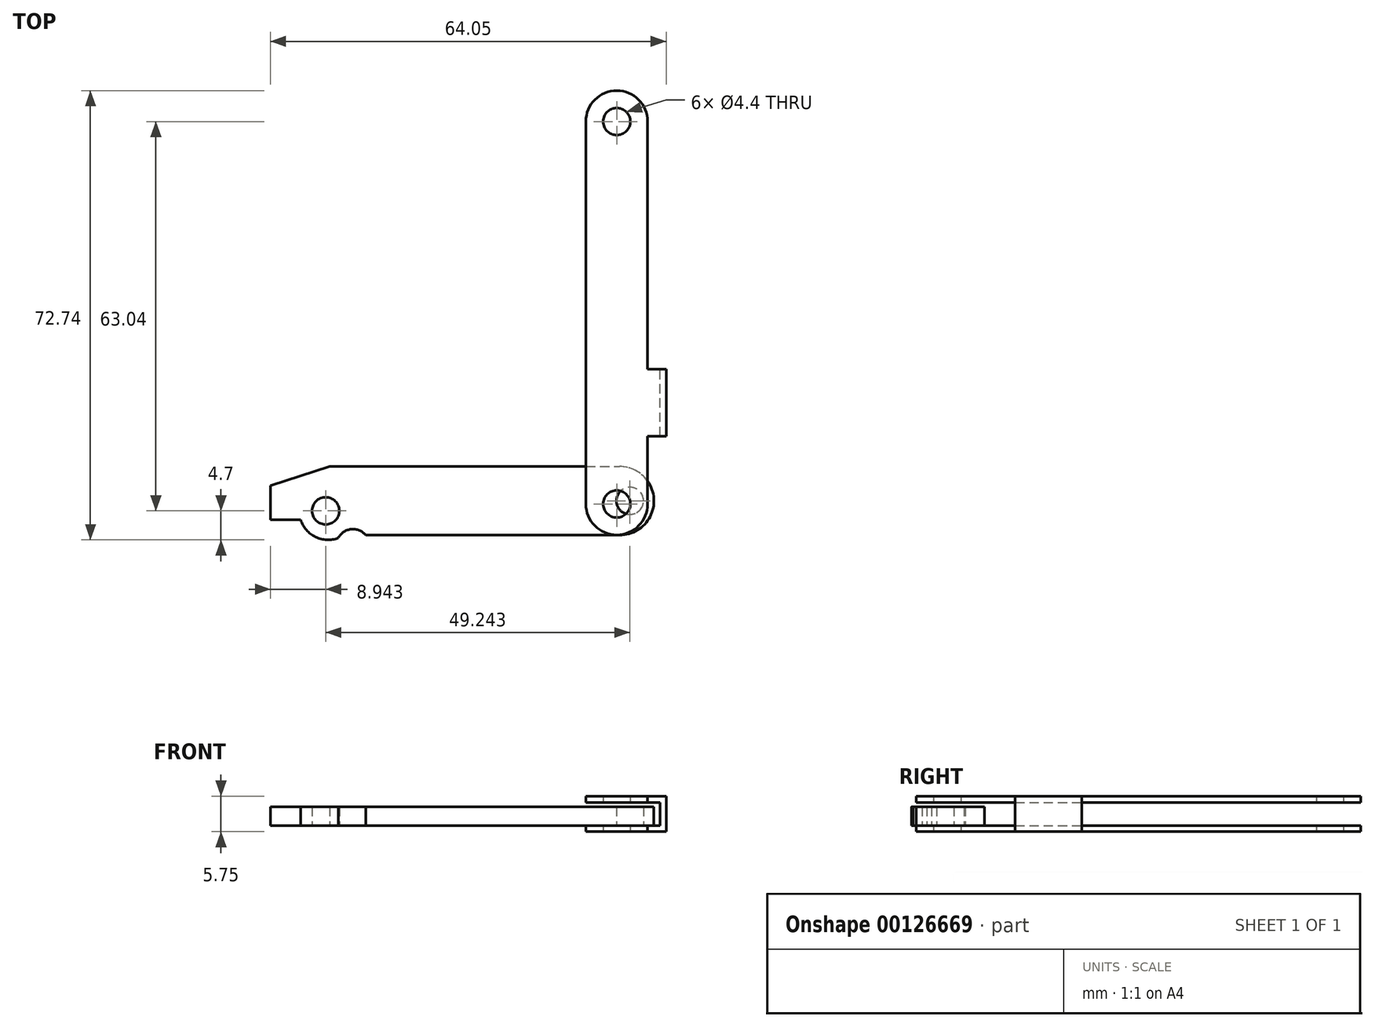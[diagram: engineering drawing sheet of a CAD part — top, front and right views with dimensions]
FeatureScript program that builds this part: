
annotation { "Feature Type Name" : "Feature", "Feature Type Description" : "" }
export const myFeature = defineFeature(function(context is Context, id is Id, definition is map)
    precondition{}
    {
        {
            var Q0;
            Q0=qCreatedBy(makeId("Top.planeOp"),FACE);
            var sketch = newSketch(context, id + "F0", { "sketchPlane" : qUnion([Q0])});
            skLineSegment(sketch, "E0", {"start": v(-5, 0) * mm, "end": v(-5, -11) * mm});
            skLineSegment(sketch, "E1", {"start": v(-5, 0) * mm, "end": v(-5, 50.93) * mm});
            skArc(sketch, "E2", {"start": v(-5, -11) * mm, "mid": v(0, -16) * mm, "end": v(5, -11) * mm});
            skLineSegment(sketch, "E3", {"start": v(5, -11) * mm, "end": v(5, 0) * mm});
            skLineSegment(sketch, "E4", {"start": v(5, 0) * mm, "end": v(7, 0) * mm});
            skLineSegment(sketch, "E5", {"start": v(7, 0) * mm, "end": v(7, 10.8) * mm});
            skLineSegment(sketch, "E6", {"start": v(7, 10.8) * mm, "end": v(5, 10.8) * mm});
            skLineSegment(sketch, "E7", {"start": v(5, 10.8) * mm, "end": v(5, 50.93) * mm});
            skArc(sketch, "E8", {"start": v(5, 50.93) * mm, "mid": v(0, 55.93) * mm, "end": v(-5, 50.93) * mm});
            skCircle(sketch, "E9", {"center": v(0, 50.93) * mm, "radius": 2.2 * mm});
            skCircle(sketch, "E10", {"center": v(0, -11) * mm, "radius": 2.2 * mm});
            skSolve(sketch);
        }
        {
            var Q0;
            Q0=makeQuery(id+"F0.imprint","IMPRINT",FACE,{"disambiguationData":[TD([[makeQuery(id+"F0.imprint","IMPRINT",EDGE,{"derivedFrom":sQuery(id+"F0.wireOp",EDGE,"E0")}),1.0]])]});
            extrude(context, id + "F1", {"entities" : qUnion([Q0]), "depth" : 3.75 * mm});
        }
        {
            var Q0;
            Q0=makeQuery(id+"F1.opExtrude","SWEPT_FACE",FACE,{"disambiguationData":[OSD([sQuery(id+"F0.wireOp",EDGE,"E0"),sQuery(id+"F0.wireOp",EDGE,"E1")])]});
            var Q1;
            Q1=makeQuery(id+"F1.opExtrude","SWEPT_FACE",FACE,{"disambiguationData":[OSD([sQuery(id+"F0.wireOp",EDGE,"E8")])]});
            var Q2;
            Q2=makeQuery(id+"F1.opExtrude","SWEPT_FACE",FACE,{"disambiguationData":[OSD([sQuery(id+"F0.wireOp",EDGE,"E2")])]});
            var Q3;
            Q3=makeQuery(id+"F1.opExtrude","SWEPT_FACE",FACE,{"disambiguationData":[OSD([sQuery(id+"F0.wireOp",EDGE,"E3")])]});
            var Q4;
            Q4=makeQuery(id+"F1.opExtrude","SWEPT_FACE",FACE,{"disambiguationData":[OSD([sQuery(id+"F0.wireOp",EDGE,"E4")])]});
            var Q5;
            Q5=makeQuery(id+"F1.opExtrude","SWEPT_FACE",FACE,{"disambiguationData":[OSD([sQuery(id+"F0.wireOp",EDGE,"E6")])]});
            var Q6;
            Q6=makeQuery(id+"F1.opExtrude","SWEPT_FACE",FACE,{"disambiguationData":[OSD([sQuery(id+"F0.wireOp",EDGE,"E7")])]});
            var Q7;
            Q7=makeQuery(id+"F1.opExtrude","SWEPT_FACE",FACE,{"disambiguationData":[OSD([sQuery(id+"F0.wireOp",EDGE,"E9")])]});
            var Q8;
            Q8=makeQuery(id+"F1.opExtrude","SWEPT_FACE",FACE,{"disambiguationData":[OSD([sQuery(id+"F0.wireOp",EDGE,"E10")])]});
            shell(context, id + "F2", {"entities" : qUnion([Q0, Q1, Q2, Q3, Q4, Q5, Q6, Q7, Q8]), "thickness" : 1 * mm, "oppositeDirection" : true});
        }
        {
            var Q0;
            Q0=qCreatedBy(makeId("Top.planeOp"),FACE);
            var sketch = newSketch(context, id + "F3", { "sketchPlane" : qUnion([Q0])});
            skLineSegment(sketch, "E11", {"start": v(-46.44, -4.94) * mm, "end": v(0.46, -4.94) * mm});
            skLineSegment(sketch, "E12", {"start": v(-46.44, -4.94) * mm, "end": v(-56.05, -8.05) * mm});
            skLineSegment(sketch, "E13", {"start": v(-56.05, -8.05) * mm, "end": v(-56.05, -13.55) * mm});
            skCircle(sketch, "E14", {"center": v(2.14, -10.5) * mm, "radius": 2.2 * mm});
            skLineSegment(sketch, "E15", {"start": v(-40.64, -16.04) * mm, "end": v(0.46, -16.04) * mm});
            skLineSegment(sketch, "E16", {"start": v(-56.05, -13.55) * mm, "end": v(-51.15, -13.55) * mm});
            skArc(sketch, "E17", {"start": v(-51.15, -13.55) * mm, "mid": v(-48.75, -16.34) * mm, "end": v(-45.07, -16.5) * mm});
            skArc(sketch, "E18", {"start": v(-40.64, -16.04) * mm, "mid": v(-42.98, -15.08) * mm, "end": v(-45.07, -16.5) * mm});
            skCircle(sketch, "E19", {"center": v(-47.1, -12.1) * mm, "radius": 2.2 * mm});
            skArc(sketch, "E20", {"start": v(0.46, -16.04) * mm, "mid": v(6.01, -10.5) * mm, "end": v(0.46, -4.94) * mm});
            skSolve(sketch);
        }
        {
            var Q0;
            Q0=makeQuery(id+"F3.imprint","IMPRINT",FACE,{"disambiguationData":[TD([[makeQuery(id+"F3.imprint","IMPRINT",EDGE,{"derivedFrom":sQuery(id+"F3.wireOp",EDGE,"E11")}),-1.0]])]});
            extrude(context, id + "F4", {"entities" : qUnion([Q0]), "depth" : 3 * mm});
        }
    });
